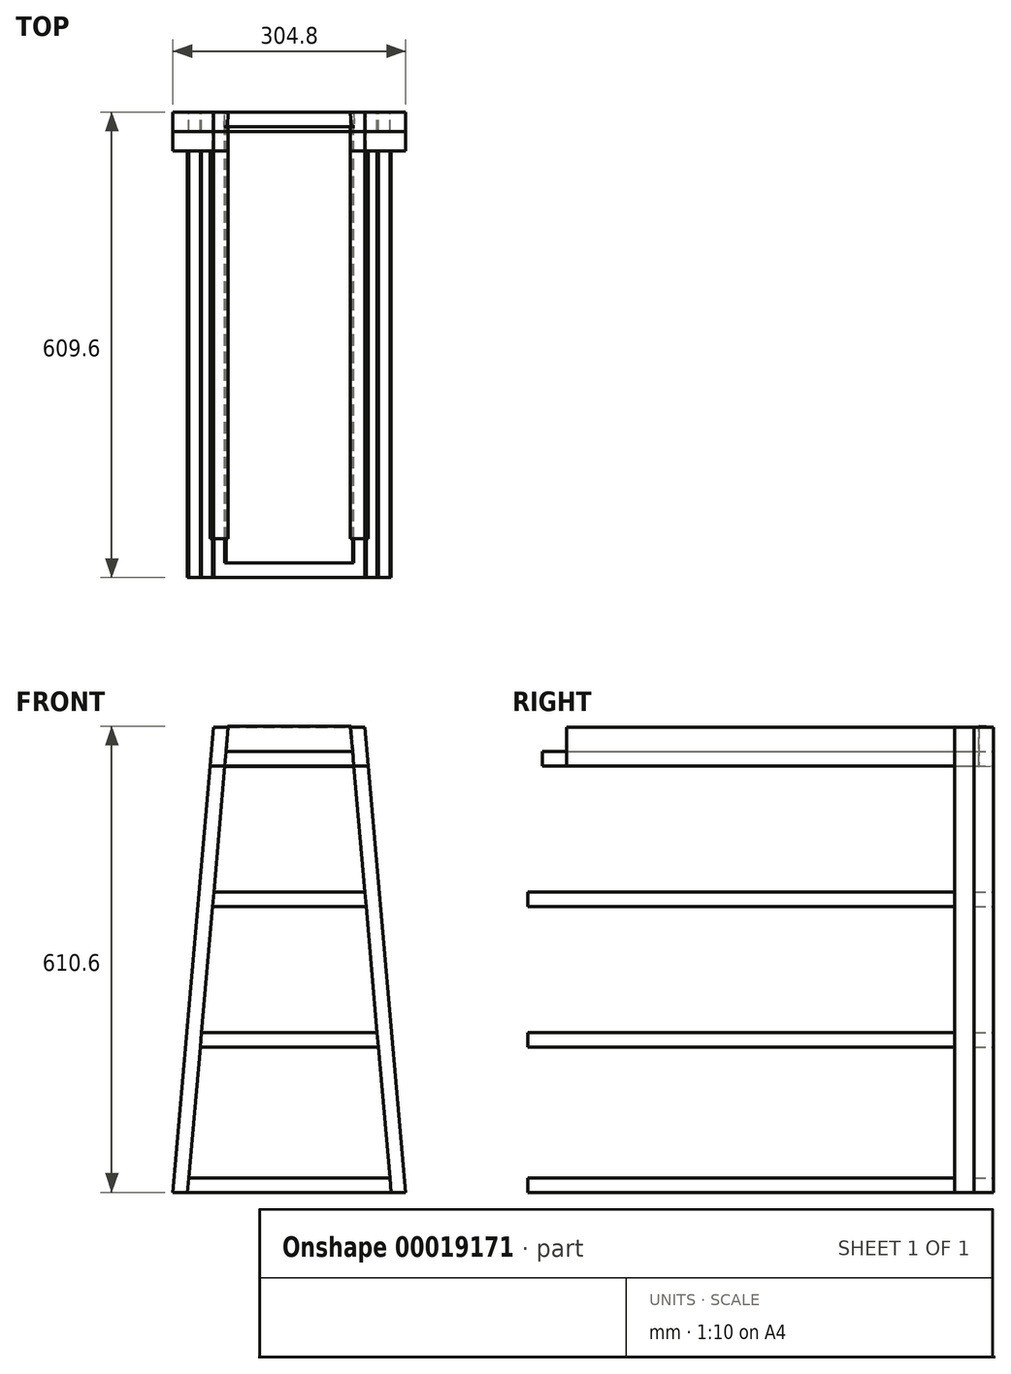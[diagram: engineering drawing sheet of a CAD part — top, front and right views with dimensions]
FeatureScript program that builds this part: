
annotation { "Feature Type Name" : "Feature", "Feature Type Description" : "" }
export const myFeature = defineFeature(function(context is Context, id is Id, definition is map)
    precondition{}
    {
        {
            var Q0;
            Q0=qCreatedBy(makeId("Front.planeOp"),FACE);
            var sketch = newSketch(context, id + "F0", { "sketchPlane" : qUnion([Q0])});
            skLineSegment(sketch, "E0", {"start": v(-133.28, 0) * mm, "end": v(-79.94, 609.6) * mm});
            skLineSegment(sketch, "E1", {"start": v(-79.94, 609.6) * mm, "end": v(-99.07, 609.6) * mm});
            skLineSegment(sketch, "E2", {"start": v(-99.07, 609.6) * mm, "end": v(-152.4, 0) * mm});
            skLineSegment(sketch, "E3", {"start": v(-152.4, 0) * mm, "end": v(-133.28, 0) * mm});
            skLineSegment(sketch, "E4", {"start": v(79.94, 609.6) * mm, "end": v(99.07, 609.6) * mm});
            skLineSegment(sketch, "E5", {"start": v(99.07, 609.6) * mm, "end": v(152.4, 0) * mm});
            skLineSegment(sketch, "E6", {"start": v(152.4, 0) * mm, "end": v(133.28, 0) * mm});
            skLineSegment(sketch, "E7", {"start": v(133.28, 0) * mm, "end": v(79.94, 609.6) * mm});
            skLineSegment(sketch, "E8", {"start": v(0, 0) * mm, "end": v(0, 818.6) * mm, "construction": true});
            skLineSegment(sketch, "E9", {"start": v(-133.28, 0) * mm, "end": v(133.28, 0) * mm});
            skLineSegment(sketch, "E10", {"start": v(-116.61, 190.5) * mm, "end": v(116.61, 190.5) * mm});
            skLineSegment(sketch, "E11", {"start": v(-100.5, 374.65) * mm, "end": v(100.5, 374.65) * mm});
            skLineSegment(sketch, "E12", {"start": v(-99.07, 609.6) * mm, "end": v(99.07, 609.6) * mm});
            skLineSegment(sketch, "E13", {"start": v(131.61, 19.05) * mm, "end": v(-131.61, 19.05) * mm});
            skLineSegment(sketch, "E14", {"start": v(114.94, 209.55) * mm, "end": v(-114.94, 209.55) * mm});
            skLineSegment(sketch, "E15", {"start": v(98.83, 393.7) * mm, "end": v(-98.83, 393.7) * mm});
            skLineSegment(sketch, "E16", {"start": v(84.39, 558.8) * mm, "end": v(-84.39, 558.8) * mm});
            skLineSegment(sketch, "E17", {"start": v(-82.72, 577.85) * mm, "end": v(82.72, 577.85) * mm});
            skLineSegment(sketch, "E18", {"start": v(-103.52, 558.73) * mm, "end": v(103.52, 558.73) * mm});
            skSolve(sketch);
        }
        {
            var Q0;
            {var subQ5=sQuery(id+"F0.wireOp",EDGE,"E3");Q0=makeQuery(id+"F0.imprint","IMPRINT",FACE,{"disambiguationData":[TD([[makeQuery(id+"F0.imprint","IMPRINT",EDGE,{"derivedFrom":subQ5}),1.0]])]});}
            var Q1;
            {var subQ3=sQuery(id+"F0.wireOp",EDGE,"E0");var subQ9=makeQuery(id+"F0.imprint","INTERSECT",VERTEX,{"derivedFrom":[subQ3,sQuery(id+"F0.wireOp",EDGE,"E15")]});Q1=makeQuery(id+"F0.imprint","IMPRINT",FACE,{"disambiguationData":[TD([[makeQuery(id+"F0.imprint","IMPRINT",EDGE,{"disambiguationData":[TD([[subQ9,1.0]])],"derivedFrom":subQ3}),1.0]])]});}
            var Q2;
            {var subQ1=sQuery(id+"F0.wireOp",EDGE,"E9");Q2=makeQuery(id+"F0.imprint","IMPRINT",FACE,{"disambiguationData":[TD([[makeQuery(id+"F0.imprint","IMPRINT",EDGE,{"derivedFrom":subQ1}),1.0]])]});}
            var Q3;
            {var subQ0=sQuery(id+"F0.wireOp",EDGE,"E14");Q3=makeQuery(id+"F0.imprint","IMPRINT",FACE,{"disambiguationData":[TD([[makeQuery(id+"F0.imprint","IMPRINT",EDGE,{"derivedFrom":subQ0}),1.0]])]});}
            var Q4;
            {var subQ0=sQuery(id+"F0.wireOp",EDGE,"E12");var subQ3=sQuery(id+"F0.wireOp",EDGE,"E5");var subQ4=makeQuery(id+"F0.imprint","INTERSECT",VERTEX,{"derivedFrom":[subQ3,subQ0]});Q4=makeQuery(id+"F0.imprint","IMPRINT",FACE,{"disambiguationData":[TD([[makeQuery(id+"F0.imprint","IMPRINT",EDGE,{"disambiguationData":[TD([[subQ4,-1.0]])],"derivedFrom":subQ3}),-1.0]])]});}
            var Q5;
            {var subQ3=sQuery(id+"F0.wireOp",EDGE,"E5");var subQ5=sQuery(id+"F0.wireOp",EDGE,"E10");var subQ7=makeQuery(id+"F0.imprint","INTERSECT",VERTEX,{"derivedFrom":[subQ3,subQ5]});Q5=makeQuery(id+"F0.imprint","IMPRINT",FACE,{"disambiguationData":[TD([[makeQuery(id+"F0.imprint","IMPRINT",EDGE,{"disambiguationData":[TD([[subQ7,1.0]])],"derivedFrom":subQ3}),-1.0]])]});}
            var Q6;
            {var subQ1=sQuery(id+"F0.wireOp",EDGE,"E0");var subQ8=makeQuery(id+"F0.imprint","INTERSECT",VERTEX,{"derivedFrom":[subQ1,sQuery(id+"F0.wireOp",EDGE,"E14")]});Q6=makeQuery(id+"F0.imprint","IMPRINT",FACE,{"disambiguationData":[TD([[makeQuery(id+"F0.imprint","IMPRINT",EDGE,{"disambiguationData":[TD([[subQ8,1.0]])],"derivedFrom":subQ1}),1.0]])]});}
            var Q7;
            {var subQ0=sQuery(id+"F0.wireOp",EDGE,"E15");Q7=makeQuery(id+"F0.imprint","IMPRINT",FACE,{"disambiguationData":[TD([[makeQuery(id+"F0.imprint","IMPRINT",EDGE,{"derivedFrom":subQ0}),1.0]])]});}
            var Q8;
            {var subQ6=sQuery(id+"F0.wireOp",EDGE,"E6");Q8=makeQuery(id+"F0.imprint","IMPRINT",FACE,{"disambiguationData":[TD([[makeQuery(id+"F0.imprint","IMPRINT",EDGE,{"derivedFrom":subQ6}),-1.0]])]});}
            var Q9;
            {var subQ0=sQuery(id+"F0.wireOp",EDGE,"E16");Q9=makeQuery(id+"F0.imprint","IMPRINT",FACE,{"disambiguationData":[TD([[makeQuery(id+"F0.imprint","IMPRINT",EDGE,{"derivedFrom":subQ0}),-1.0]])]});}
            var Q10;
            {var subQ1=sQuery(id+"F0.wireOp",EDGE,"E0");var subQ9=makeQuery(id+"F0.imprint","INTERSECT",VERTEX,{"derivedFrom":[subQ1,sQuery(id+"F0.wireOp",EDGE,"E16")]});Q10=makeQuery(id+"F0.imprint","IMPRINT",FACE,{"disambiguationData":[TD([[makeQuery(id+"F0.imprint","IMPRINT",EDGE,{"disambiguationData":[TD([[subQ9,1.0]])],"derivedFrom":subQ1}),1.0]])]});}
            extrude(context, id + "F1", {"entities" : qUnion([Q0, Q1, Q2, Q3, Q4, Q5, Q6, Q7, Q8, Q9, Q10]), "depth" : 25.4 * mm});
        }
        {
            var Q0;
            {var subQ1=sQuery(id+"F0.wireOp",EDGE,"E2");Q0=makeQuery(id+"F0.imprint","IMPRINT",FACE,{"disambiguationData":[TD([[makeQuery(id+"F0.imprint","IMPRINT",EDGE,{"derivedFrom":subQ1}),1.0]])]});}
            var Q1;
            {var subQ3=sQuery(id+"F0.wireOp",EDGE,"E5");Q1=makeQuery(id+"F0.imprint","IMPRINT",FACE,{"disambiguationData":[TD([[makeQuery(id+"F0.imprint","IMPRINT",EDGE,{"derivedFrom":subQ3}),-1.0]])]});}
            var Q2;
            {var subQ5=sQuery(id+"F0.wireOp",EDGE,"E3");Q2=makeQuery(id+"F0.imprint","IMPRINT",FACE,{"disambiguationData":[TD([[makeQuery(id+"F0.imprint","IMPRINT",EDGE,{"derivedFrom":subQ5}),1.0]])]});}
            var Q3;
            {var subQ10=sQuery(id+"F0.wireOp",EDGE,"E6");Q3=makeQuery(id+"F0.imprint","IMPRINT",FACE,{"disambiguationData":[TD([[makeQuery(id+"F0.imprint","IMPRINT",EDGE,{"derivedFrom":subQ10}),-1.0]])]});}
            extrude(context, id + "F2", {"entities" : qUnion([Q0, Q1, Q2, Q3]), "depth" : 50.8 * mm});
        }
        {
            var Q0;
            {var subQ1=sQuery(id+"F0.wireOp",EDGE,"E9");Q0=makeQuery(id+"F0.imprint","IMPRINT",FACE,{"disambiguationData":[TD([[makeQuery(id+"F0.imprint","IMPRINT",EDGE,{"derivedFrom":subQ1}),1.0]])]});}
            var Q1;
            {var subQ1=sQuery(id+"F0.wireOp",EDGE,"E11");Q1=makeQuery(id+"F0.imprint","IMPRINT",FACE,{"disambiguationData":[TD([[makeQuery(id+"F0.imprint","IMPRINT",EDGE,{"derivedFrom":subQ1}),1.0]])]});}
            var Q2;
            {var subQ1=sQuery(id+"F0.wireOp",EDGE,"E10");Q2=makeQuery(id+"F0.imprint","IMPRINT",FACE,{"disambiguationData":[TD([[makeQuery(id+"F0.imprint","IMPRINT",EDGE,{"derivedFrom":subQ1}),1.0]])]});}
            extrude(context, id + "F3", {"entities" : qUnion([Q0, Q1, Q2]), "depth" : 609.6 * mm});
        }
        {
            var Q0;
            {var subQ1=sQuery(id+"F0.wireOp",EDGE,"E16");Q0=makeQuery(id+"F0.imprint","IMPRINT",FACE,{"disambiguationData":[TD([[makeQuery(id+"F0.imprint","IMPRINT",EDGE,{"derivedFrom":subQ1}),-1.0]])]});}
            extrude(context, id + "F4", {"entities" : qUnion([Q0]), "depth" : 590.55 * mm, "hasSecondDirection" : true, "secondDirectionOppositeDirection" : false, "secondDirectionDepth" : 19.05 * mm});
        }
        {
            var Q0;
            {var subQ1=sQuery(id+"F0.wireOp",EDGE,"E0");var subQ9=makeQuery(id+"F0.imprint","INTERSECT",VERTEX,{"derivedFrom":[subQ1,sQuery(id+"F0.wireOp",EDGE,"E16")]});Q0=makeQuery(id+"F0.imprint","IMPRINT",FACE,{"disambiguationData":[TD([[makeQuery(id+"F0.imprint","IMPRINT",EDGE,{"disambiguationData":[TD([[subQ9,1.0]])],"derivedFrom":subQ1}),1.0]])]});}
            var Q1;
            {var subQ3=sQuery(id+"F0.wireOp",EDGE,"E5");var subQ5=sQuery(id+"F0.wireOp",EDGE,"E12");var subQ7=makeQuery(id+"F0.imprint","INTERSECT",VERTEX,{"derivedFrom":[subQ3,subQ5]});Q1=makeQuery(id+"F0.imprint","IMPRINT",FACE,{"disambiguationData":[TD([[makeQuery(id+"F0.imprint","IMPRINT",EDGE,{"disambiguationData":[TD([[subQ7,-1.0]])],"derivedFrom":subQ3}),-1.0]])]});}
            extrude(context, id + "F5", {"entities" : qUnion([Q0, Q1]), "depth" : 558.8 * mm, "hasSecondDirection" : true, "secondDirectionOppositeDirection" : false, "secondDirectionDepth" : 50.8 * mm});
        }
        {
            var Q0;
            {var subQ1=sQuery(id+"F0.wireOp",EDGE,"E16");Q0=makeQuery(id+"F0.imprint","IMPRINT",FACE,{"disambiguationData":[TD([[makeQuery(id+"F0.imprint","IMPRINT",EDGE,{"derivedFrom":subQ1}),-1.0]])]});}
            var Q1;
            {var subQ0=sQuery(id+"F0.wireOp",EDGE,"E17");Q1=makeQuery(id+"F0.imprint","IMPRINT",FACE,{"disambiguationData":[TD([[makeQuery(id+"F0.imprint","IMPRINT",EDGE,{"derivedFrom":subQ0}),1.0]])]});}
            extrude(context, id + "F6", {"entities" : qUnion([Q0, Q1]), "depth" : 19.05 * mm, "hasDraft" : true, "draftAngle" : 3 * degree});
        }
    });
